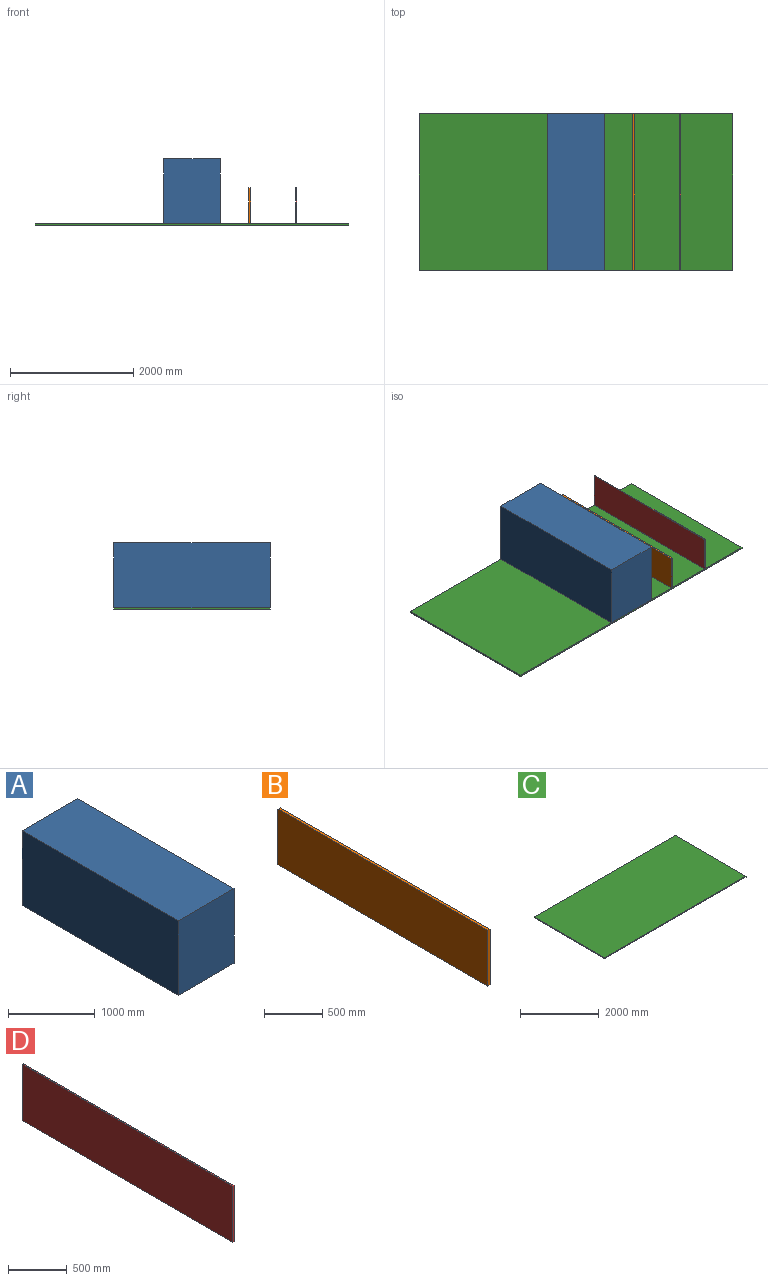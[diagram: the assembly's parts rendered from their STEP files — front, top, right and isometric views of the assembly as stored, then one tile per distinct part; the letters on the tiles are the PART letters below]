
ASSEMBLY  parts=4 mates=3
PART A: 6 faces, bbox 909.7x2540x1051.6 mm
  f0: plane 2540x1051.56mm, normal (-1,0,0), area 2670962.4mm2, adj f1,f3,f4,f5
  f1: plane 1051.56x909.73mm, normal (0,-1,0), area 956634.7mm2, adj f0,f2,f4,f5
  f2: plane 2540x1051.56mm, normal (1,0,0), area 2670962.4mm2, adj f1,f3,f4,f5
  f3: plane 1051.56x909.73mm, normal (0,1,0), area 956634.7mm2, adj f0,f2,f4,f5
  f4: plane 2540x909.73mm, normal (0,0,1), area 2310711.9mm2, adj f0,f1,f2,f3
  f5: plane 2540x909.73mm, normal (0,0,-1), area 2310711.9mm2, adj f0,f1,f2,f3
PART B: 6 faces, bbox 25.4x2540x584.2 mm
  f0: plane 584.2x25.4mm, normal (0,-1,0), area 14838.7mm2, adj f1,f3,f4,f5
  f1: plane 2540x584.2mm, normal (1,0,0), area 1483868mm2, adj f0,f2,f4,f5
  f2: plane 584.2x25.4mm, normal (0,1,0), area 14838.7mm2, adj f1,f3,f4,f5
  f3: plane 2540x584.2mm, normal (-1,0,0), area 1483868mm2, adj f0,f2,f4,f5
  f4: plane 2540x25.4mm, normal (0,0,1), area 64516mm2, adj f0,f1,f2,f3
  f5: plane 2540x25.4mm, normal (0,0,-1), area 64516mm2, adj f0,f1,f2,f3
PART C: 6 faces, bbox 5080x2540x25.4 mm
  f0: plane 5080x25.4mm, normal (0,1,0), area 129032mm2, adj f1,f3,f4,f5
  f1: plane 2540x25.4mm, normal (-1,0,0), area 64516mm2, adj f0,f2,f4,f5
  f2: plane 5080x25.4mm, normal (0,-1,0), area 129032mm2, adj f1,f3,f4,f5
  f3: plane 2540x25.4mm, normal (1,0,0), area 64516mm2, adj f0,f2,f4,f5
  f4: plane 5080x2540mm, normal (0,0,1), area 12903200mm2, adj f0,f1,f2,f3
  f5: plane 5080x2540mm, normal (0,0,-1), area 12903200mm2, adj f0,f1,f2,f3
PART D: 6 faces, bbox 12.7x2540x584.2 mm
  f0: plane 584.2x12.7mm, normal (0,1,0), area 7419.3mm2, adj f1,f3,f4,f5
  f1: plane 2540x584.2mm, normal (-1,0,0), area 1483868mm2, adj f0,f2,f4,f5
  f2: plane 584.2x12.7mm, normal (0,-1,0), area 7419.3mm2, adj f1,f3,f4,f5
  f3: plane 2540x584.2mm, normal (1,0,0), area 1483868mm2, adj f0,f2,f4,f5
  f4: plane 2540x12.7mm, normal (0,0,1), area 32258mm2, adj f0,f1,f2,f3
  f5: plane 2540x12.7mm, normal (0,0,-1), area 32258mm2, adj f0,f1,f2,f3
PLACE A t=(667.92,353.19,-33.87)mm
PLACE B t=(488.77,353.19,-33.87)mm
PLACE C t=(-19.19,353.19,-33.87)mm
PLACE D t=(468.94,353.19,-33.87)mm
MATE planar B.f5 <-> C.f4  axis (0,0,-1) through (939.76,-12.67,-8.47)mm
MATE planar A.f5 <-> C.f4  axis (0,0,-1) through (2.5,-12.67,-8.47)mm
MATE planar D.f5 <-> C.f4  axis (0,0,-1) through (1694.14,-12.67,-8.47)mm
